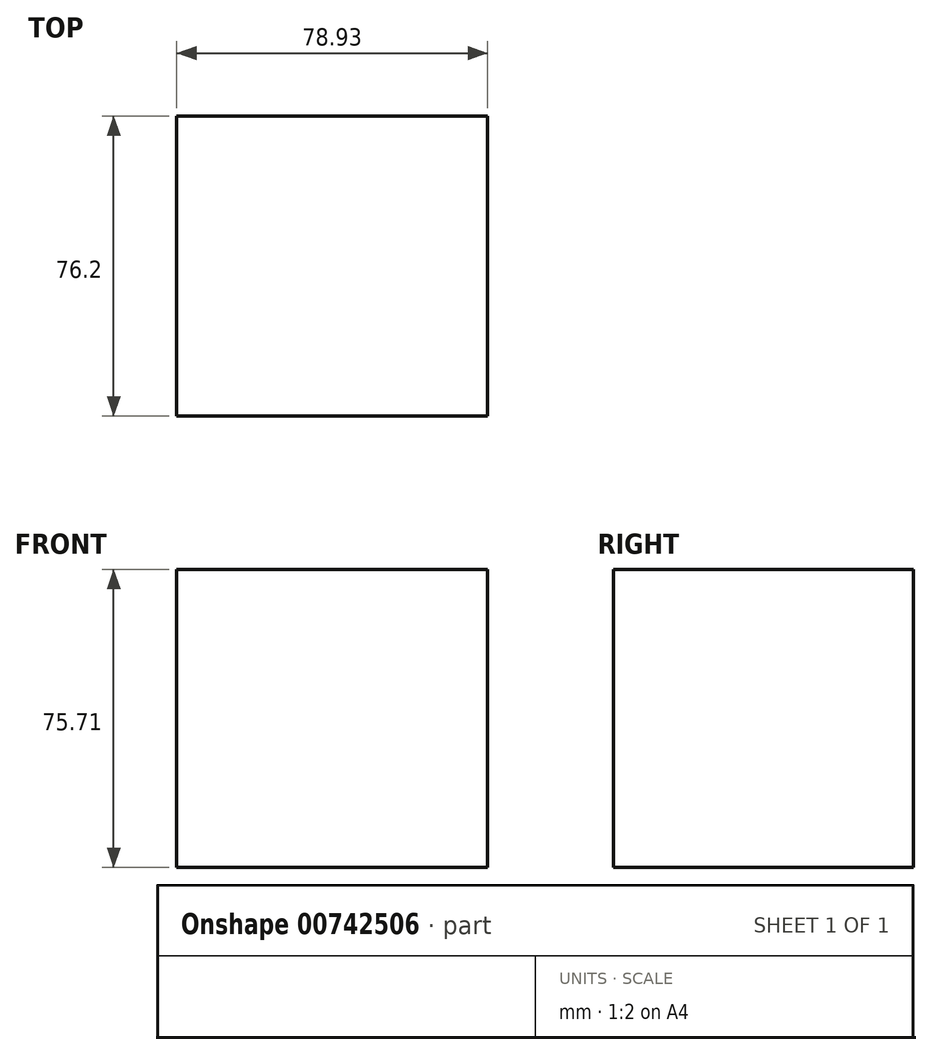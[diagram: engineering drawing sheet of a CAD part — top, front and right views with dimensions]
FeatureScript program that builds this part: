
annotation { "Feature Type Name" : "Feature", "Feature Type Description" : "" }
export const myFeature = defineFeature(function(context is Context, id is Id, definition is map)
    precondition{}
    {
        {
            var Q0;
            Q0=qCreatedBy(makeId("Front.planeOp"),FACE);
            var sketch = newSketch(context, id + "F0", { "sketchPlane" : qUnion([Q0])});
            skLineSegment(sketch, "E0.bottom", {"start": v(15.93, 36.47) * mm, "end": v(94.86, 36.47) * mm});
            skLineSegment(sketch, "E0.top", {"start": v(15.93, -39.24) * mm, "end": v(94.86, -39.24) * mm});
            skLineSegment(sketch, "E0.left", {"start": v(15.93, 36.47) * mm, "end": v(15.93, -39.24) * mm});
            skLineSegment(sketch, "E0.right", {"start": v(94.86, 36.47) * mm, "end": v(94.86, -39.24) * mm});
            skSolve(sketch);
        }
        {
            var Q0;
            Q0 = qSketchRegion(id + "F0", true);
            extrude(context, id + "F1", {"entities" : qUnion([Q0]), "depth" : 76.2 * mm, "offsetDistance" : 25.4 * mm});
        }
    });
